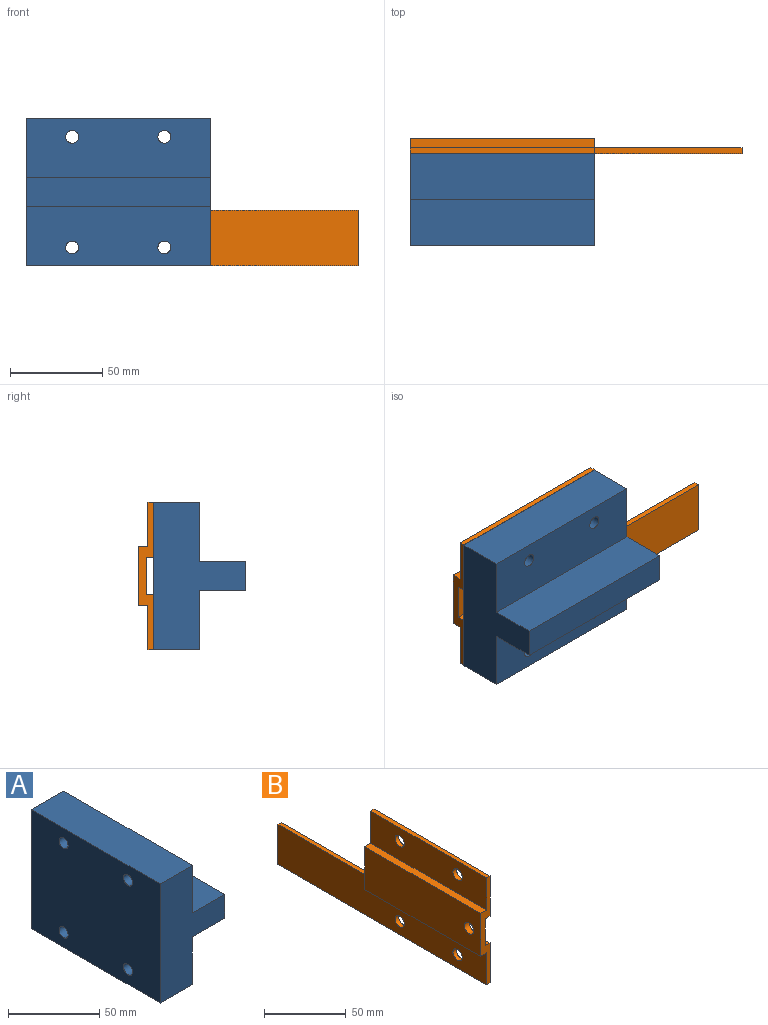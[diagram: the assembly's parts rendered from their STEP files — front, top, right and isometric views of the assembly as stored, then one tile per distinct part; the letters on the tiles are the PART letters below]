
ASSEMBLY  parts=2 mates=1
PART A: 14 faces, bbox 50x100x80 mm
  f0: plane 100x25mm, normal (0,0,1), area 2500mm2, adj f1,f7,f8,f9
  f1: plane 100x32mm, normal (1,0,0), area 3123mm2, adj f0,f2,f8,f9,f12,f13
  f2: plane 100x25mm, normal (0,0,1), area 2500mm2, adj f1,f3,f8,f9
  f3: plane 100x80mm, normal (-1,0,0), area 7846.1mm2, adj f2,f4,f8,f9,f10,f11,f12,f13
  f4: plane 100x25mm, normal (0,0,-1), area 2500mm2, adj f3,f5,f8,f9
  f5: plane 100x32mm, normal (1,0,0), area 3123mm2, adj f4,f6,f8,f9,f10,f11
  f6: plane 100x25mm, normal (0,0,-1), area 2500mm2, adj f5,f7,f8,f9
  f7: plane 100x16mm, normal (1,0,0), area 1600mm2, adj f0,f6,f8,f9
  f8: plane 80x50mm, normal (0,-1,0), area 2400mm2, adj f0,f1,f2,f3,f4,f5,f6,f7
  f9: plane 80x50mm, normal (0,1,0), area 2400mm2, adj f0,f1,f2,f3,f4,f5,f6,f7
  f10: cylinder r=3.5mm len=25mm, axis (-1,0,0), area 549.8mm2, adj f3,f5
  f11: cylinder r=3.5mm len=25mm, axis (-1,0,0), area 549.8mm2, adj f3,f5
  f12: cylinder r=3.5mm len=25mm, axis (-1,0,0), area 549.8mm2, adj f1,f3
  f13: cylinder r=3.5mm len=25mm, axis (-1,0,0), area 549.8mm2, adj f1,f3
PART B: 20 faces, bbox 8.2x180x80 mm
  f0: plane 100x3mm, normal (0,0,1), area 300mm2, adj f4,f5,f12,f19
  f1: plane 100x32mm, normal (-1,0,0), area 3149.7mm2, adj f6,f7,f12,f16,f19
  f2: plane 100x20mm, normal (1,0,0), area 1949.7mm2, adj f3,f11,f12,f16,f19
  f3: plane 100x4mm, normal (0,0,-1), area 400mm2, adj f2,f4,f12,f19
  f4: plane 100x30mm, normal (1,0,0), area 2899.5mm2, adj f0,f3,f12,f14,f15,f19
  f5: plane 100x24mm, normal (-1,0,0), area 2299.5mm2, adj f0,f6,f12,f14,f15,f19
  f6: plane 100x5.19mm, normal (0,0,1), area 519mm2, adj f1,f5,f12,f19
  f7: plane 100x5.19mm, normal (0,0,-1), area 519mm2, adj f1,f8,f12,f19
  f8: plane 180x30mm, normal (-1,0,0), area 4699.5mm2, adj f7,f9,f11,f12,f13,f17,f18,f19
  f9: plane 180x3mm, normal (0,0,-1), area 540mm2, adj f8,f10,f12,f13
  f10: plane 180x30mm, normal (1,0,0), area 5299.5mm2, adj f9,f11,f12,f13,f17,f18
  f11: plane 180x4mm, normal (0,0,1), area 640mm2, adj f2,f8,f10,f12,f13,f19
  f12: plane 80x8.19mm, normal (0,-1,0), area 326.1mm2, adj f0,f1,f2,f3,f4,f5,f6,f7
  f13: plane 30x3mm, normal (0,1,0), area 90mm2, adj f8,f9,f10,f11
  f14: cylinder r=4mm len=8mm, axis (-1,0,0), area 75.4mm2, adj f4,f5
  f15: cylinder r=4mm len=8mm, axis (-1,0,0), area 75.4mm2, adj f4,f5
  f16: cylinder r=4mm len=8mm, axis (-1,0,0), area 105.3mm2, adj f1,f2
  f17: cylinder r=4mm len=8mm, axis (-1,0,0), area 75.4mm2, adj f8,f10
  f18: cylinder r=4mm len=8mm, axis (-1,0,0), area 75.4mm2, adj f8,f10
  f19: plane 56x8.19mm, normal (0,1,0), area 236.1mm2, adj f0,f1,f2,f3,f4,f5,f6,f7
PLACE A rot(axis=(0,0,-1),90deg) t=(-16.2,25.6,-11.75)mm
PLACE B rot(axis=(0,0,-1),90deg) t=(63.8,23.41,-11.57)mm
MATE parallel B.f4 <-> A.f3  axis (0,-1,0) through (-66.2,20.41,13.25)mm
